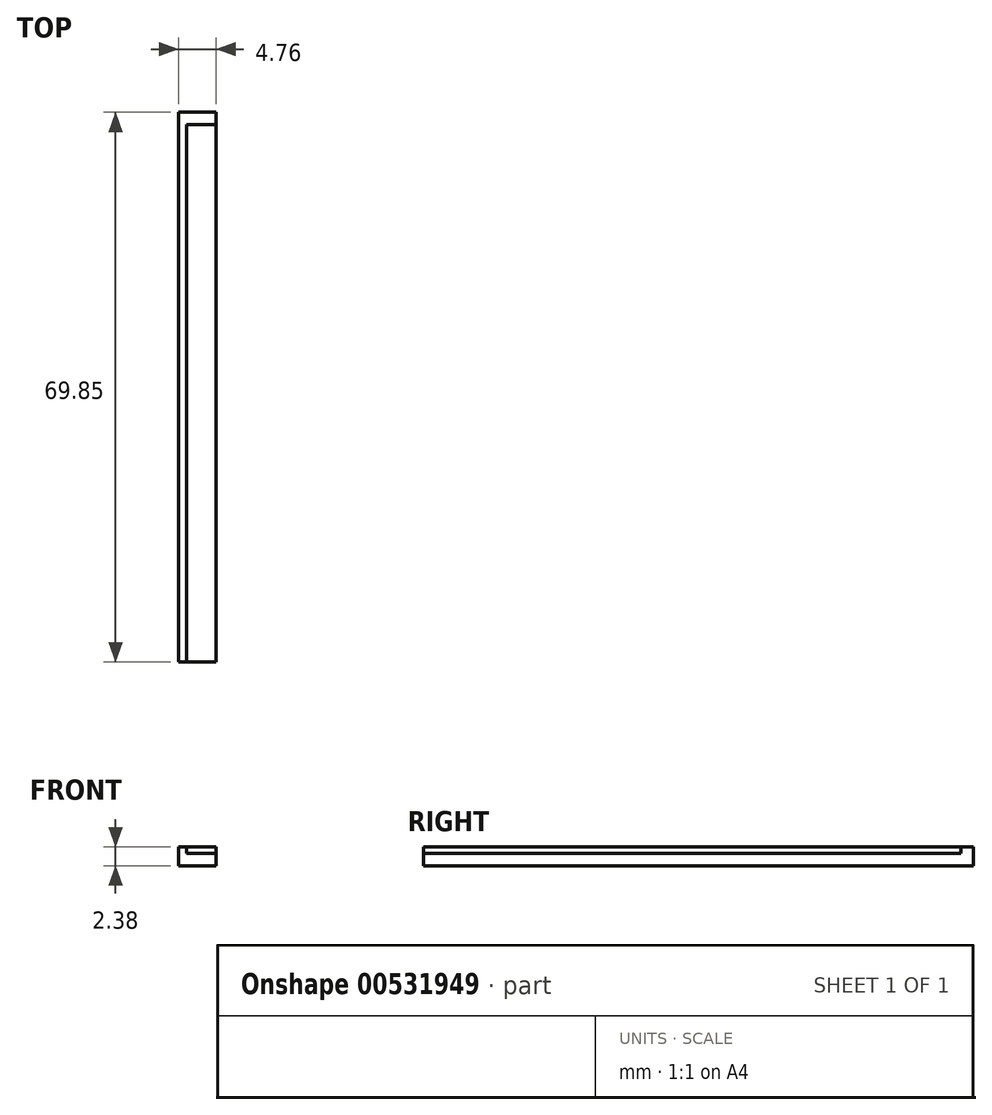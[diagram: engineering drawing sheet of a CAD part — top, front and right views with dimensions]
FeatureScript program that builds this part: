
annotation { "Feature Type Name" : "Feature", "Feature Type Description" : "" }
export const myFeature = defineFeature(function(context is Context, id is Id, definition is map)
    precondition{}
    {
        {
            var Q0;
            Q0=qCreatedBy(makeId("Top.planeOp"),FACE);
            var sketch = newSketch(context, id + "F0", { "sketchPlane" : qUnion([Q0])});
            skLineSegment(sketch, "E0.bottom", {"start": v(-29.98, 52.98) * mm, "end": v(-25.22, 52.98) * mm});
            skLineSegment(sketch, "E0.top", {"start": v(-29.98, -16.87) * mm, "end": v(-25.22, -16.87) * mm});
            skLineSegment(sketch, "E0.left", {"start": v(-29.98, 52.98) * mm, "end": v(-29.98, -16.87) * mm});
            skLineSegment(sketch, "E0.right", {"start": v(-25.22, 52.98) * mm, "end": v(-25.22, -16.87) * mm});
            skLineSegment(sketch, "E1", {"start": v(-29.98, 51.39) * mm, "end": v(-25.22, 51.39) * mm});
            skLineSegment(sketch, "E2", {"start": v(-28.94, 52.98) * mm, "end": v(-28.94, -16.87) * mm});
            skSolve(sketch);
        }
        {
            var Q0;
            {var subQ0=sQuery(id+"F0.wireOp",EDGE,"E0.left");var subQ1=sQuery(id+"F0.wireOp",EDGE,"E0.bottom");var subQ2=makeQuery(id+"F0.imprint","INTERSECT",VERTEX,{"derivedFrom":[subQ1,subQ0]});Q0=makeQuery(id+"F0.imprint","IMPRINT",FACE,{"disambiguationData":[TD([[makeQuery(id+"F0.imprint","IMPRINT",EDGE,{"disambiguationData":[TD([[subQ2,-1.0]])],"derivedFrom":subQ1}),-1.0]])]});}
            var Q1;
            {var subQ0=sQuery(id+"F0.wireOp",EDGE,"E0.right");var subQ1=sQuery(id+"F0.wireOp",EDGE,"E0.bottom");var subQ2=makeQuery(id+"F0.imprint","INTERSECT",VERTEX,{"derivedFrom":[subQ1,subQ0]});Q1=makeQuery(id+"F0.imprint","IMPRINT",FACE,{"disambiguationData":[TD([[makeQuery(id+"F0.imprint","IMPRINT",EDGE,{"disambiguationData":[TD([[subQ2,1.0]])],"derivedFrom":subQ1}),-1.0]])]});}
            var Q2;
            {var subQ0=sQuery(id+"F0.wireOp",EDGE,"E0.left");var subQ1=sQuery(id+"F0.wireOp",EDGE,"E0.top");var subQ2=makeQuery(id+"F0.imprint","INTERSECT",VERTEX,{"derivedFrom":[subQ1,subQ0]});Q2=makeQuery(id+"F0.imprint","IMPRINT",FACE,{"disambiguationData":[TD([[makeQuery(id+"F0.imprint","IMPRINT",EDGE,{"disambiguationData":[TD([[subQ2,-1.0]])],"derivedFrom":subQ1}),1.0]])]});}
            extrude(context, id + "F1", {"entities" : qUnion([Q0, Q1, Q2]), "depth" : 2.38 * mm, "offsetDistance" : 25.4 * mm});
        }
        {
            var Q0;
            {var subQ0=sQuery(id+"F0.wireOp",EDGE,"E0.right");var subQ1=sQuery(id+"F0.wireOp",EDGE,"E0.top");var subQ2=makeQuery(id+"F0.imprint","INTERSECT",VERTEX,{"derivedFrom":[subQ1,subQ0]});Q0=makeQuery(id+"F0.imprint","IMPRINT",FACE,{"disambiguationData":[TD([[makeQuery(id+"F0.imprint","IMPRINT",EDGE,{"disambiguationData":[TD([[subQ2,1.0]])],"derivedFrom":subQ1}),1.0]])]});}
            extrude(context, id + "F2", {"entities" : qUnion([Q0]), "operationType" : NewBodyOperationType.ADD, "depth" : 1.59 * mm, "offsetDistance" : 25.4 * mm});
        }
    });
